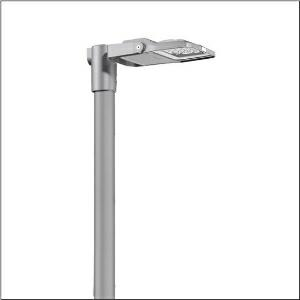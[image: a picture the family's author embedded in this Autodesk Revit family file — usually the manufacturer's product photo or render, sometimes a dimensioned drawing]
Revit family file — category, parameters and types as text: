
# Revit family: floodlight_fl_21_micro___pl43_5xa7761a2a3a_b6d3
name_source: partatom
category: Lighting Fixtures
units: mm (PartAtom-declared; Revit-internal decimal feet)

## family parameters
Cut with Voids When Loaded = No
Host = Face
Light Source = No
Part Type = Normal
Room Calculation Point = No
Round Connector Dimension = Use Diameter
Shared = No

## types (1)
- --- (1 x LED, 3040 lm, 23.1 W, 3000K)
    Apparent Load = 23 VA
    CIE Flux Codes = 29 80 99 100 100
    Color Rendering = 70
    Color Temperature = 3000K
    Default Elevation = 1800 mm
    Description = Floodlight FL 21 micro, floodlight, primary light control with lens, of PMMA, primary optical cover: protective disc, of toughened safety glass, transparent, light distribution: PL43, light emission: direct distribution, installation type: surface-mounted, LED, High Power LED, rated luminous flux: 3.040lm, luminous efficacy: 132lm/W, light colour: 730, colour temperature: 3000K, control gear: ECG iQ, control: optimised constant luminous flux control (CLO 2.0), Desk-Remote (wireless, voltage-free reading and setting of iQ features in the workshop via application-optimized NFC function/RFID function), Light-Fading, Smart-Wire, Night-Set, Lumen-Switch, Temp-Guard, Auto-Match, with terminal, 6-pole, mains connection: 220..240V, AC, 50/60Hz, start of lifetime: 23W, end of lifetime: 24W, reduction: 11W, luminaire housing, of diecast aluminium, powder-coated, Siteco® metallic grey (DB 702S), corrosivity category C5 according to DIN EN ISO 12944, mast bracket, of steel, galvanised, powder-coated, Siteco® metallic grey (DB 702S), protection rating (complete): IP66, insulation class (complete): insulation class II (safety insulation), certification: CE, protection symbol: D, impact resistance: IK07, permissible operating ambient temperature: -40..+40°C, permissible operating ambient temperature for outdoor applications: -40..+50°C, standard: DIN EN 12944, packaging unit: 1 piece

Light Distribution: PL43
    Height = 65 mm
    Lamp = 1 x LED
    Lamp Light Flux = 3040 lm
    Lamp Power = 23.1 W
    Lamp count = 1
    Length = 312 mm
    Luminous efficacy = 132 lm/W
    Manufacturer = Siteco
    ModVariant = No
    Model = 5XA7761A2A3A
    Number of Poles = 1
    OnlyDefault = Yes
    Power Factor = 1
    Product Name = Floodlight FL 21 micro | PL43
    Product group = floodlight | pylon top
    ProductGroupID = 6101
    Protection Class = Protection class II
    Protection Degree = IP 66
    RLX_Detail_Level = 1
    RlxData = <blob elided: 101665 chars, md5=1dae7078>
    Socket = socket
    Standby Power = 0 W
    System Light Flux = 3040 lm
    System Power = 23 W
    Type Comments = factory setting: luminous flux: 100 % | dim-lin: 254 | 455 mA
    Type Image = l_1007121.jpg
    URL = http://relux.com
    VarID = @adj_090109
    Voltage = 0 V
    Weight = 0.00 kg
    Width = 230 mm

## geometry (parser evidence)
native form markers: Blend x4, Sweep x13
no freeform markers — native parametric forms only
